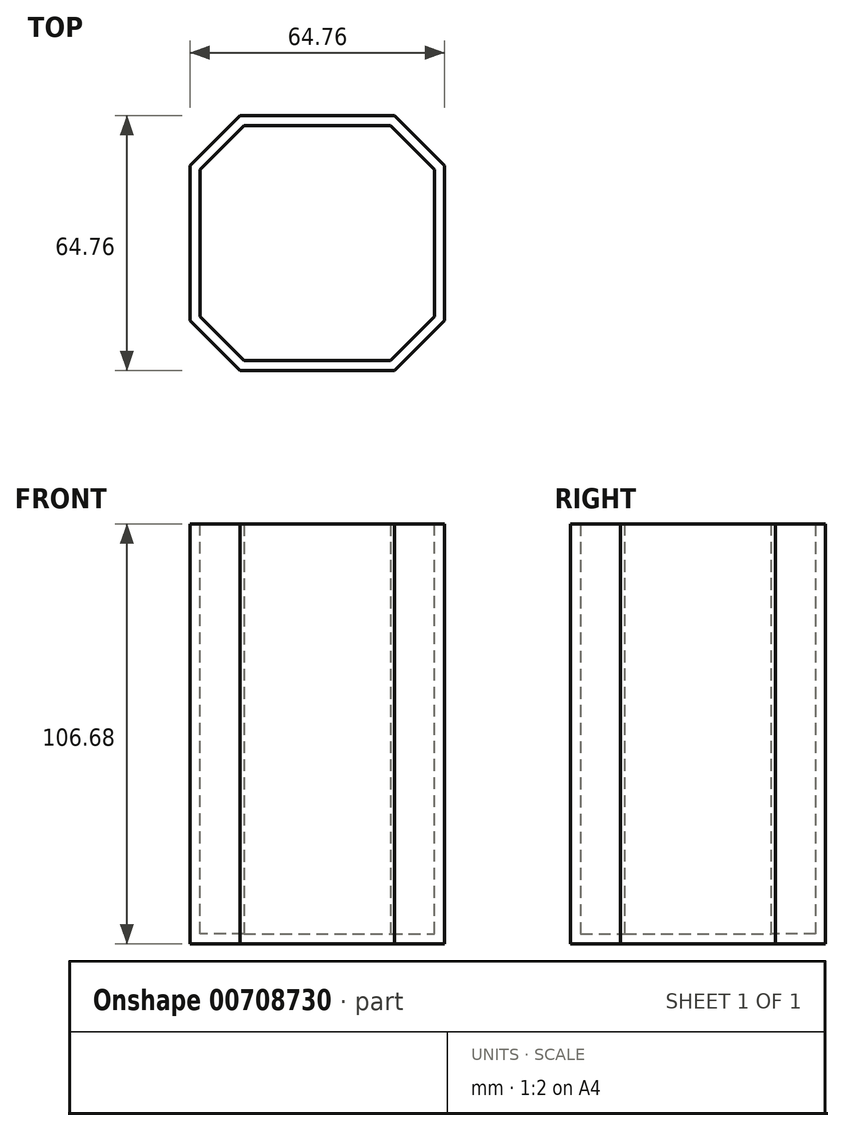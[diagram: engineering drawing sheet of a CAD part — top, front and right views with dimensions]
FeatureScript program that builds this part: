
annotation { "Feature Type Name" : "Feature", "Feature Type Description" : "" }
export const myFeature = defineFeature(function(context is Context, id is Id, definition is map)
    precondition{}
    {
        {
            var Q0;
            Q0=qCreatedBy(makeId("Top.planeOp"),FACE);
            var sketch = newSketch(context, id + "F0", { "sketchPlane" : qUnion([Q0])});
            skLineSegment(sketch, "E0.bottom", {"start": v(-32.38, -32.38) * mm, "end": v(32.38, -32.38) * mm});
            skLineSegment(sketch, "E0.top", {"start": v(-32.38, 32.38) * mm, "end": v(32.38, 32.38) * mm});
            skLineSegment(sketch, "E0.left", {"start": v(-32.38, -32.38) * mm, "end": v(-32.38, 32.38) * mm});
            skLineSegment(sketch, "E0.right", {"start": v(32.38, -32.38) * mm, "end": v(32.38, 32.38) * mm});
            skPoint(sketch, "E0.middle", {"position": v(0, 0) * mm});
            skSolve(sketch);
        }
        {
            var Q0;
            Q0=makeQuery(id+"F0.imprint","IMPRINT",FACE,{"disambiguationData":[TD([[makeQuery(id+"F0.imprint","IMPRINT",EDGE,{"derivedFrom":sQuery(id+"F0.wireOp",EDGE,"E0.bottom")}),1.0]])]});
            extrude(context, id + "F1", {"entities" : qUnion([Q0]), "depth" : 53.34 * mm, "offsetDistance" : 25.4 * mm});
        }
        {
            var Q0;
            Q0=makeQuery(id+"F1.opExtrude","CAP_FACE",FACE,{"disambiguationData":[OSD([sQuery(id+"F0.wireOp",EDGE,"E0.bottom"),sQuery(id+"F0.wireOp",EDGE,"E0.top"),sQuery(id+"F0.wireOp",EDGE,"E0.left"),sQuery(id+"F0.wireOp",EDGE,"E0.right")])],"isStart":true});
            extrude(context, id + "F2", {"entities" : qUnion([Q0]), "operationType" : NewBodyOperationType.ADD, "depth" : 53.34 * mm, "offsetDistance" : 25.4 * mm});
        }
        {
            var Q0;
            {var subQ0=sQuery(id+"F0.wireOp",EDGE,"E0.left");var subQ1=sQuery(id+"F0.wireOp",EDGE,"E0.bottom");Q0=makeQuery(id+"F2.boolean.opBoolean","MERGE",EDGE,{"derivedFrom":[makeQuery(id+"F1.opExtrude","SWEPT_EDGE",EDGE,{"disambiguationData":[OSD([subQ1,subQ0])]}),makeQuery(id+"F2.opExtrude","SWEPT_EDGE",EDGE,{"disambiguationData":[OSD([subQ1,subQ0])]})]});}
            chamfer(context, id + "F3", {"entities" : qUnion([Q0]), "width" : 12.7 * mm, "tangentPropagation" : true});
        }
        {
            var Q0;
            {var subQ0=sQuery(id+"F0.wireOp",EDGE,"E0.left");var subQ1=sQuery(id+"F0.wireOp",EDGE,"E0.top");Q0=makeQuery(id+"F2.boolean.opBoolean","MERGE",EDGE,{"derivedFrom":[makeQuery(id+"F1.opExtrude","SWEPT_EDGE",EDGE,{"disambiguationData":[OSD([subQ1,subQ0])]}),makeQuery(id+"F2.opExtrude","SWEPT_EDGE",EDGE,{"disambiguationData":[OSD([subQ1,subQ0])]})]});}
            chamfer(context, id + "F4", {"entities" : qUnion([Q0]), "width" : 12.7 * mm, "tangentPropagation" : true});
        }
        {
            var Q0;
            {var subQ0=sQuery(id+"F0.wireOp",EDGE,"E0.right");var subQ1=sQuery(id+"F0.wireOp",EDGE,"E0.top");Q0=makeQuery(id+"F2.boolean.opBoolean","MERGE",EDGE,{"derivedFrom":[makeQuery(id+"F1.opExtrude","SWEPT_EDGE",EDGE,{"disambiguationData":[OSD([subQ1,subQ0])]}),makeQuery(id+"F2.opExtrude","SWEPT_EDGE",EDGE,{"disambiguationData":[OSD([subQ1,subQ0])]})]});}
            chamfer(context, id + "F5", {"entities" : qUnion([Q0]), "width" : 12.7 * mm, "tangentPropagation" : true});
        }
        {
            var Q0;
            {var subQ0=sQuery(id+"F0.wireOp",EDGE,"E0.right");var subQ1=sQuery(id+"F0.wireOp",EDGE,"E0.bottom");Q0=makeQuery(id+"F2.boolean.opBoolean","MERGE",EDGE,{"derivedFrom":[makeQuery(id+"F1.opExtrude","SWEPT_EDGE",EDGE,{"disambiguationData":[OSD([subQ1,subQ0])]}),makeQuery(id+"F2.opExtrude","SWEPT_EDGE",EDGE,{"disambiguationData":[OSD([subQ1,subQ0])]})]});}
            chamfer(context, id + "F6", {"entities" : qUnion([Q0]), "width" : 12.7 * mm, "tangentPropagation" : true});
        }
        {
            var Q0;
            Q0=makeQuery(id+"F1.opExtrude","CAP_FACE",FACE,{"disambiguationData":[OSD([sQuery(id+"F0.wireOp",EDGE,"E0.bottom"),sQuery(id+"F0.wireOp",EDGE,"E0.top"),sQuery(id+"F0.wireOp",EDGE,"E0.left"),sQuery(id+"F0.wireOp",EDGE,"E0.right")])],"isStart":false});
            shell(context, id + "F7", {"entities" : qUnion([Q0]), "thickness" : 2.54 * mm});
        }
    });
